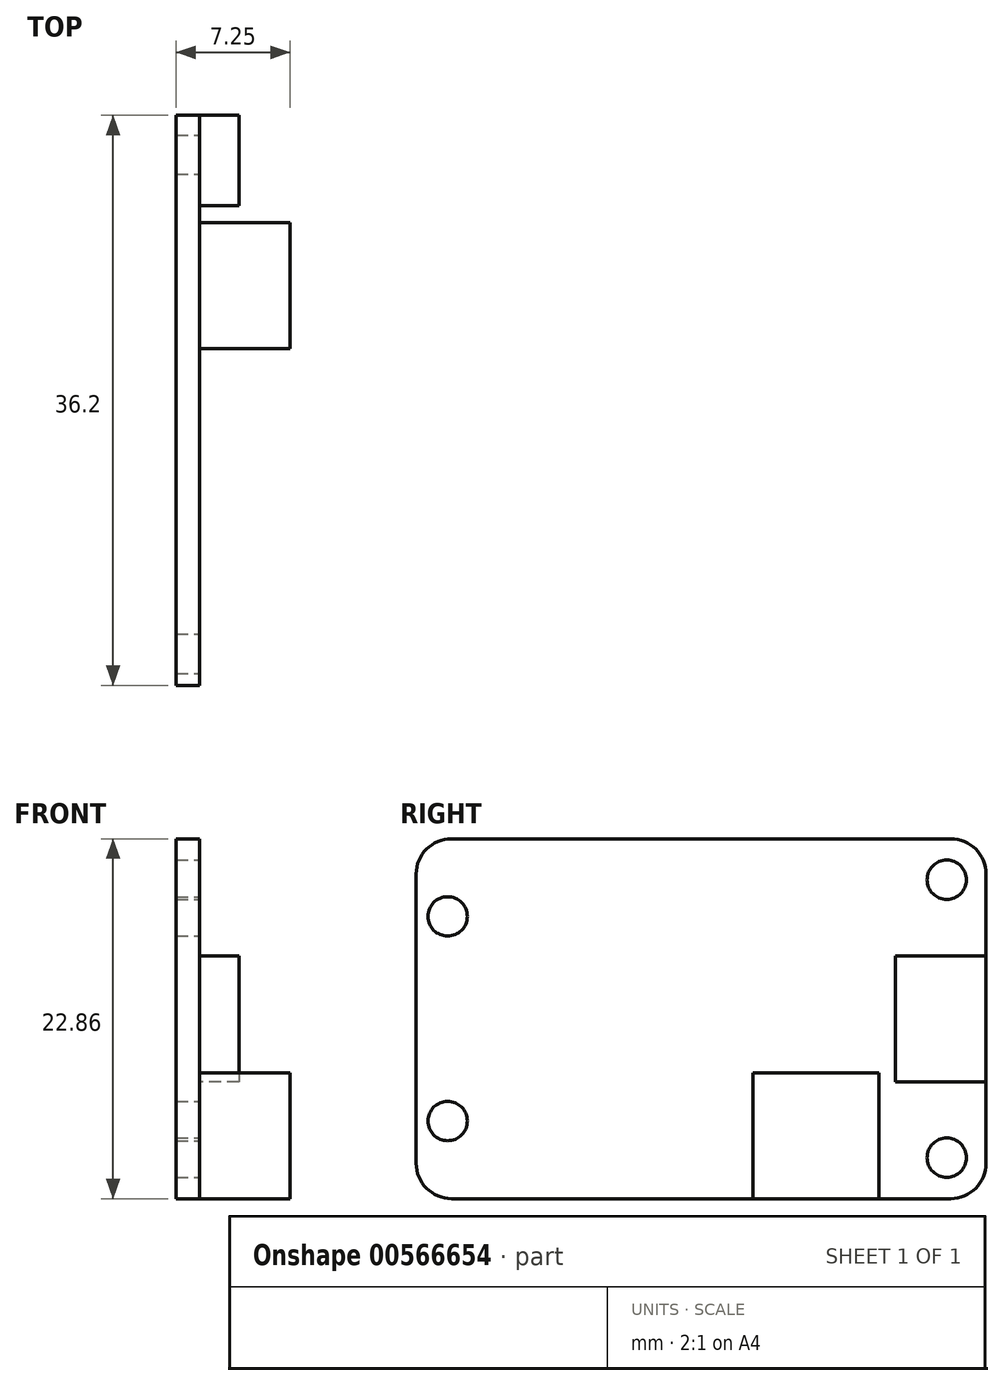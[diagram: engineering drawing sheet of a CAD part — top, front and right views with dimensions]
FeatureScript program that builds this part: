
annotation { "Feature Type Name" : "Feature", "Feature Type Description" : "" }
export const myFeature = defineFeature(function(context is Context, id is Id, definition is map)
    precondition{}
    {
        {
            var Q0;
            Q0=qCreatedBy(makeId("Right.planeOp"),FACE);
            var sketch = newSketch(context, id + "F0", { "sketchPlane" : qUnion([Q0])});
            skLineSegment(sketch, "E0.bottom", {"start": v(-18.1, 11.43) * mm, "end": v(18.1, 11.43) * mm});
            skLineSegment(sketch, "E0.top", {"start": v(-18.1, -11.43) * mm, "end": v(18.1, -11.43) * mm});
            skLineSegment(sketch, "E0.left", {"start": v(-18.1, 11.43) * mm, "end": v(-18.1, -11.43) * mm});
            skLineSegment(sketch, "E0.right", {"start": v(18.1, 11.43) * mm, "end": v(18.1, -11.43) * mm});
            skPoint(sketch, "E0.middle", {"position": v(0, 0) * mm});
            skSolve(sketch);
        }
        {
            var Q0;
            Q0=makeQuery(id+"F0.imprint","IMPRINT",FACE,{"disambiguationData":[TD([[makeQuery(id+"F0.imprint","IMPRINT",EDGE,{"derivedFrom":sQuery(id+"F0.wireOp",EDGE,"E0.bottom")}),-1.0]])]});
            extrude(context, id + "F1", {"entities" : qUnion([Q0]), "endBound" : BoundingType.SYMMETRIC, "depth" : 1.5 * mm, "offsetDistance" : 25 * mm});
        }
        {
            var Q0;
            Q0=makeQuery(id+"F1.opExtrude","CAP_FACE",FACE,{"disambiguationData":[OSD([sQuery(id+"F0.wireOp",EDGE,"E0.bottom"),sQuery(id+"F0.wireOp",EDGE,"E0.top"),sQuery(id+"F0.wireOp",EDGE,"E0.left"),sQuery(id+"F0.wireOp",EDGE,"E0.right")])],"isStart":false});
            var sketch = newSketch(context, id + "F2", { "sketchPlane" : qUnion([Q0])});
            skLineSegment(sketch, "E1.bottom", {"start": v(11.3, -11.43) * mm, "end": v(3.3, -11.43) * mm});
            skLineSegment(sketch, "E1.top", {"start": v(11.3, -3.43) * mm, "end": v(3.3, -3.43) * mm});
            skLineSegment(sketch, "E1.left", {"start": v(11.3, -11.43) * mm, "end": v(11.3, -3.43) * mm});
            skLineSegment(sketch, "E1.right", {"start": v(3.3, -11.43) * mm, "end": v(3.3, -3.43) * mm});
            skLineSegment(sketch, "E2.bottom", {"start": v(18.1, 4) * mm, "end": v(12.35, 4) * mm});
            skLineSegment(sketch, "E2.top", {"start": v(18.1, -4) * mm, "end": v(12.35, -4) * mm});
            skLineSegment(sketch, "E2.left", {"start": v(18.1, 4) * mm, "end": v(18.1, -4) * mm});
            skLineSegment(sketch, "E2.right", {"start": v(12.35, 4) * mm, "end": v(12.35, -4) * mm});
            skPoint(sketch, "E2.middle", {"position": v(15.23, 0) * mm});
            skSolve(sketch);
        }
        {
            var Q0;
            Q0=makeQuery(id+"F2.imprint","IMPRINT",FACE,{"disambiguationData":[TD([[makeQuery(id+"F2.imprint","IMPRINT",EDGE,{"derivedFrom":sQuery(id+"F2.wireOp",EDGE,"E1.bottom")}),1.0]])]});
            extrude(context, id + "F3", {"entities" : qUnion([Q0]), "operationType" : NewBodyOperationType.ADD, "depth" : 5.75 * mm, "offsetDistance" : 25 * mm});
        }
        {
            var Q0;
            Q0=makeQuery(id+"F2.imprint","IMPRINT",FACE,{"disambiguationData":[TD([[makeQuery(id+"F2.imprint","IMPRINT",EDGE,{"derivedFrom":sQuery(id+"F2.wireOp",EDGE,"E2.bottom")}),1.0]])]});
            extrude(context, id + "F4", {"entities" : qUnion([Q0]), "operationType" : NewBodyOperationType.ADD, "depth" : 2.5 * mm, "offsetDistance" : 25 * mm});
        }
        {
            var Q0;
            Q0=makeQuery(id+"F1.opExtrude","SWEPT_EDGE",EDGE,{"disambiguationData":[OSD([sQuery(id+"F0.wireOp",EDGE,"E0.bottom"),sQuery(id+"F0.wireOp",EDGE,"E0.left")])]});
            var Q1;
            Q1=makeQuery(id+"F1.opExtrude","SWEPT_EDGE",EDGE,{"disambiguationData":[OSD([sQuery(id+"F0.wireOp",EDGE,"E0.bottom"),sQuery(id+"F0.wireOp",EDGE,"E0.right")])]});
            var Q2;
            Q2=makeQuery(id+"F1.opExtrude","SWEPT_EDGE",EDGE,{"disambiguationData":[OSD([sQuery(id+"F0.wireOp",EDGE,"E0.top"),sQuery(id+"F0.wireOp",EDGE,"E0.right")])]});
            var Q3;
            Q3=makeQuery(id+"F1.opExtrude","SWEPT_EDGE",EDGE,{"disambiguationData":[OSD([sQuery(id+"F0.wireOp",EDGE,"E0.top"),sQuery(id+"F0.wireOp",EDGE,"E0.left")])]});
            fillet(context, id + "F5", {"entities" : qUnion([Q0, Q1, Q2, Q3]), "radius" : 2.25 * mm, "tangentPropagation" : true, "allowEdgeOverflow" : false});
        }
        {
            var Q0;
            Q0=makeQuery(id+"F2.imprint","IMPRINT",FACE,{"disambiguationData":[TD([[makeQuery(id+"F2.imprint","IMPRINT",EDGE,{"derivedFrom":sQuery(id+"F2.wireOp",EDGE,"E1.top")}),-1.0]])]});
            var sketch = newSketch(context, id + "F6", { "sketchPlane" : qUnion([Q0])});
            skCircle(sketch, "E3", {"center": v(15.6, 8.82) * mm, "radius": 1.25 * mm});
            skCircle(sketch, "E4", {"center": v(15.6, -8.83) * mm, "radius": 1.25 * mm});
            skCircle(sketch, "E5", {"center": v(-16.1, 6.5) * mm, "radius": 1.25 * mm});
            skCircle(sketch, "E6", {"center": v(-16.1, -6.5) * mm, "radius": 1.25 * mm});
            skSolve(sketch);
        }
        {
            var Q0;
            Q0=qSketchRegion(id+"F6",true);
            var Q1;
            Q1=makeQuery(id+"F1.opExtrude","CAP_FACE",FACE,{"disambiguationData":[OSD([sQuery(id+"F0.wireOp",EDGE,"E0.bottom"),sQuery(id+"F0.wireOp",EDGE,"E0.top"),sQuery(id+"F0.wireOp",EDGE,"E0.left"),sQuery(id+"F0.wireOp",EDGE,"E0.right")])],"isStart":true});
            extrude(context, id + "F7", {"entities" : qUnion([Q0]), "operationType" : NewBodyOperationType.REMOVE, "endBound" : BoundingType.UP_TO_SURFACE, "oppositeDirection" : true, "depth" : 25 * mm, "endBoundEntityFace" : qUnion([Q1]), "offsetDistance" : 25 * mm});
        }
    });
